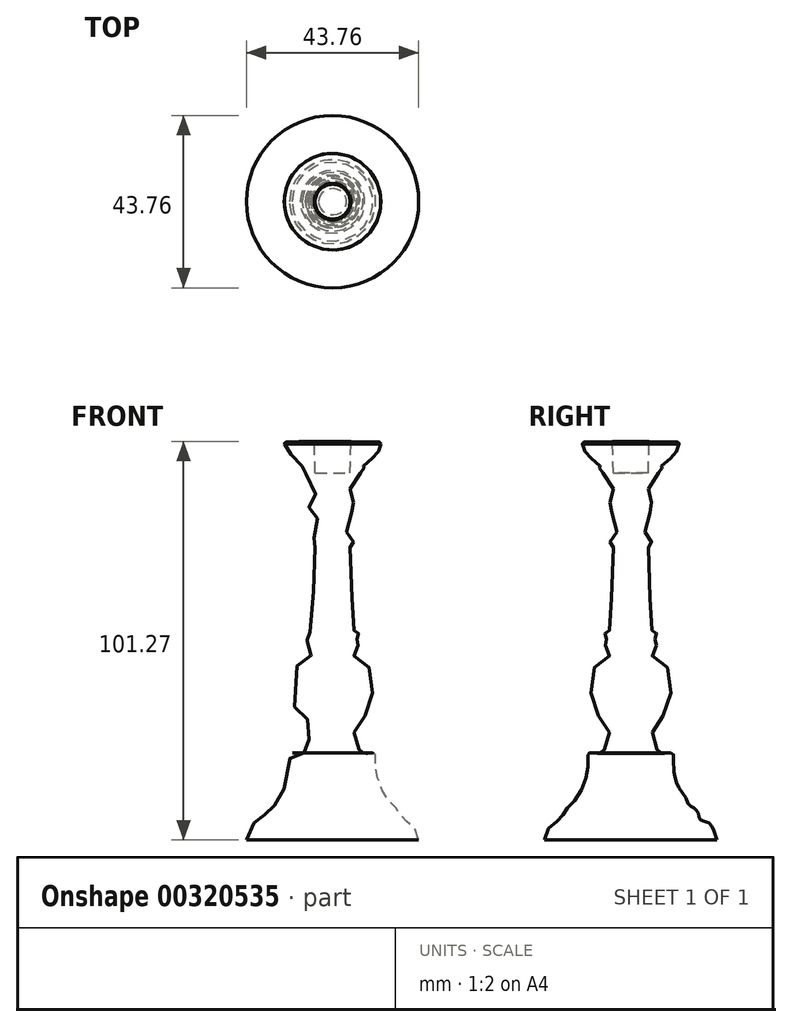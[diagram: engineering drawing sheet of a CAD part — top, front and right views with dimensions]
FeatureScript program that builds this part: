
annotation { "Feature Type Name" : "Feature", "Feature Type Description" : "" }
export const myFeature = defineFeature(function(context is Context, id is Id, definition is map)
    precondition{}
    {
        {
            var Q0;
            Q0=qCreatedBy(makeId("Front.planeOp"),FACE);
            var sketch = newSketch(context, id + "F0", { "sketchPlane" : qUnion([Q0])});
            skFitSpline(sketch, "E0", {"points": [v(-12.16, 46.22) * mm, v(-12.09, 44.22) * mm, v(-10.78, 43.37) * mm, v(-10.47, 42.6) * mm, v(-8.7, 40.9) * mm, v(-7.62, 39.82) * mm, v(-8.08, 39.51) * mm, v(-7.54, 38.82) * mm, v(-5.15, 36.35) * mm, v(-4.46, 32.2) * mm, v(-5.46, 30.73) * mm, v(-6, 29.57) * mm, v(-5.15, 28.5) * mm, v(-3.92, 27.1) * mm, v(-3.76, 22.86) * mm, v(-5.07, 21.48) * mm, v(-5.15, 20.55) * mm, v(-4.46, 19.7) * mm, v(-4.53, 18.93) * mm, v(-5.46, -1.65) * mm, v(-6, -2.03) * mm, v(-6.61, -2.57) * mm, v(-6.15, -3.58) * mm, v(-6.77, -4.73) * mm, v(-5.69, -6.66) * mm, v(-5.84, -8.9) * mm, v(-8.54, -9.82) * mm, v(-9.47, -21.7) * mm, v(-7.3, -23.77) * mm, v(-6, -24.77) * mm, v(-5.69, -28.78) * mm, v(-6.85, -30.56) * mm, v(-6.85, -32.48) * mm, v(-10.62, -32.8) * mm, v(-10.85, -33.25) * mm, v(-11.62, -40.35) * mm, v(-14.25, -44.66) * mm, v(-14.7, -46.05) * mm, v(-16.1, -46.74) * mm, v(-17.17, -48.2) * mm, v(-17.64, -49.67) * mm, v(-19.49, -50.29) * mm, v(-20.72, -51.6) * mm, v(-21.88, -54.84) * mm], "startDerivative": vector(-19.72, -106.26) * mm, "endDerivative": vector(-38.26, -124.88) * mm});
            skLineSegment(sketch, "E1", {"start": v(-21.88, -54.84) * mm, "end": v(0, -54.84) * mm});
            skLineSegment(sketch, "E2", {"start": v(0, -54.84) * mm, "end": v(0, 38.35) * mm});
            skLineSegment(sketch, "E3.trimOffspring", {"start": v(0, -54.84) * mm, "end": v(0, -73.73) * mm, "construction": true});
            skPoint(sketch, "E4.end.orphan", {"position": v(0, 46.55) * mm});
            skPoint(sketch, "E4.start.orphan", {"position": v(0, 67.87) * mm});
            skPoint(sketch, "E5.start.orphan", {"position": v(-6.08, 46.39) * mm});
            skLineSegment(sketch, "E6", {"start": v(-12.16, 46.22) * mm, "end": v(-4.65, 46.43) * mm});
            skLineSegment(sketch, "E7", {"start": v(-3.1, 38.35) * mm, "end": v(0, 38.35) * mm});
            skPoint(sketch, "E8.orphan", {"position": v(0, 41.32) * mm});
            skLineSegment(sketch, "E9", {"start": v(-4.65, 46.43) * mm, "end": v(-4.43, 38.35) * mm});
            skLineSegment(sketch, "E10", {"start": v(-4.43, 38.35) * mm, "end": v(-3.1, 38.35) * mm});
            skSolve(sketch);
        }
        {
            var Q0;
            Q0 = qSketchRegion(id + "F0", true);
            var Q1;
            Q1=sQuery(id+"F0.wireOp",EDGE,"E2");
            revolve(context, id + "F1", {"entities" : qUnion([Q0]), "axis" : qUnion([Q1]), "revolveType" : RevolveType.FULL});
        }
        {
            var Q0;
            Q0=makeQuery(id+"F1.opRevolve","SWEPT_EDGE",EDGE,{"disambiguationData":[OSD([sQuery(id+"F0.wireOp",EDGE,"E0"),sQuery(id+"F0.wireOp",EDGE,"E6")])]});
            fillet(context, id + "F2", {"entities" : qUnion([Q0]), "radius" : 0.5 * mm, "tangentPropagation" : true, "allowEdgeOverflow" : false});
        }
    });
